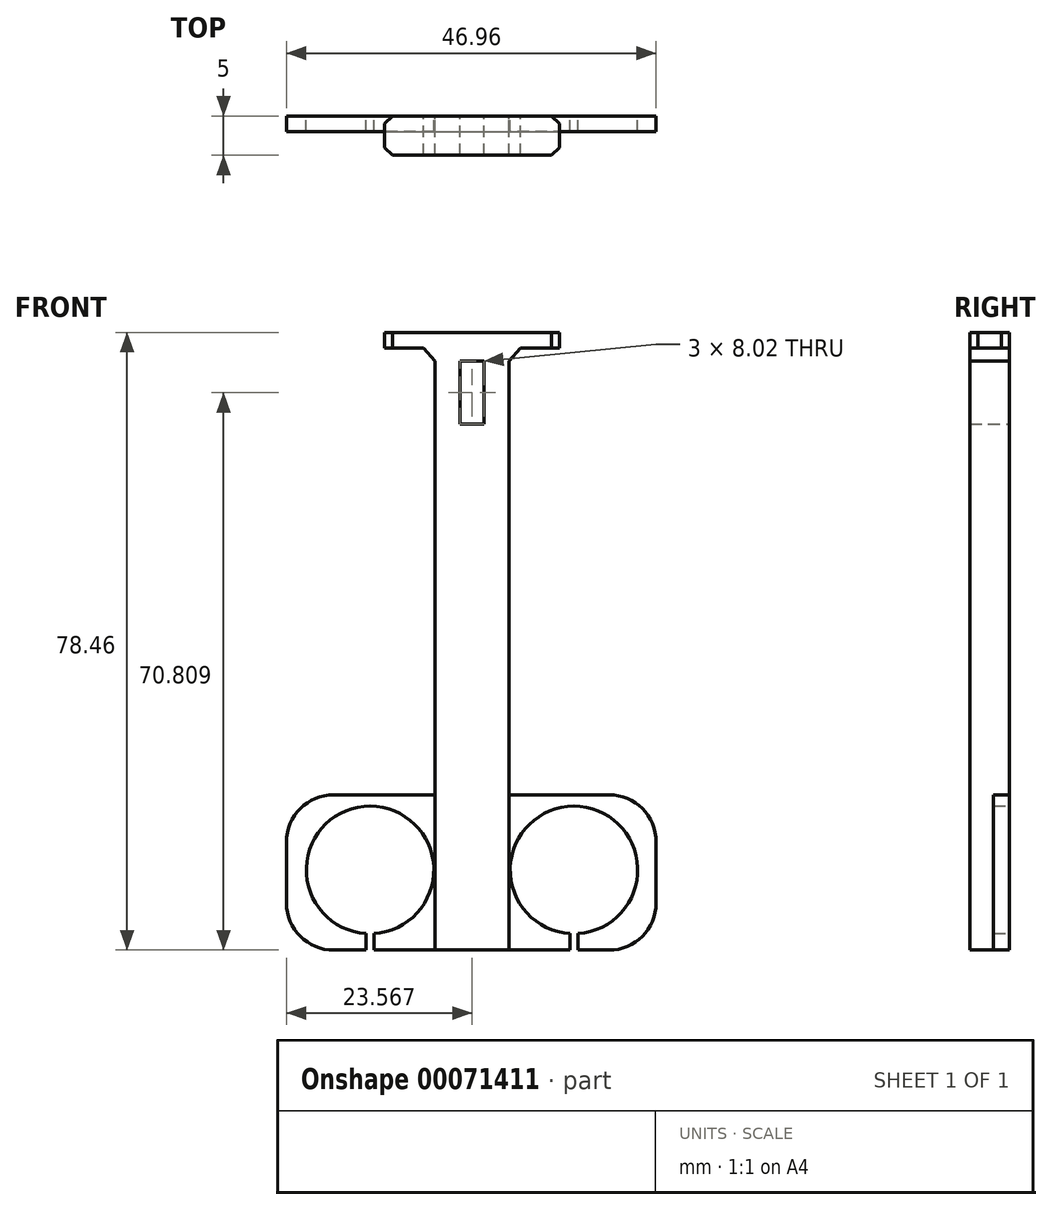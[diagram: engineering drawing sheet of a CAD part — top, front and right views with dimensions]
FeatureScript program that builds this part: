
annotation { "Feature Type Name" : "Feature", "Feature Type Description" : "" }
export const myFeature = defineFeature(function(context is Context, id is Id, definition is map)
    precondition{}
    {
        {
            var Q0;
            Q0=qCreatedBy(makeId("Front.planeOp"),FACE);
            var sketch = newSketch(context, id + "F0", { "sketchPlane" : qUnion([Q0])});
            skLineSegment(sketch, "E0.bottom", {"start": v(-5.27, 61.35) * mm, "end": v(4.07, 61.35) * mm});
            skLineSegment(sketch, "E0.top", {"start": v(-5.27, -13.44) * mm, "end": v(4.07, -13.44) * mm});
            skLineSegment(sketch, "E0.left", {"start": v(-5.27, 61.35) * mm, "end": v(-5.27, -13.44) * mm});
            skLineSegment(sketch, "E0.right", {"start": v(4.07, 61.35) * mm, "end": v(4.07, -13.44) * mm});
            skLineSegment(sketch, "E1", {"start": v(-3.37, -13.44) * mm, "end": v(-3.37, 61.35) * mm});
            skLineSegment(sketch, "E2", {"start": v(2.17, 61.35) * mm, "end": v(2.17, -13.44) * mm});
            skArc(sketch, "E3", {"start": v(-13.07, -11.37) * mm, "mid": v(-13.53, 4.81) * mm, "end": v(-14.07, -11.37) * mm});
            skArc(sketch, "E4.MirrorC", {"start": v(11.87, -11.37) * mm, "mid": v(12.33, 4.81) * mm, "end": v(12.87, -11.37) * mm});
            skLineSegment(sketch, "E5.bottom", {"start": v(-18.17, 6.25) * mm, "end": v(16.8, 6.25) * mm});
            skLineSegment(sketch, "E5.top", {"start": v(-18.17, -13.47) * mm, "end": v(-14.07, -13.47) * mm});
            skLineSegment(sketch, "E5.left", {"start": v(-24.17, 0.25) * mm, "end": v(-24.17, -7.47) * mm});
            skLineSegment(sketch, "E5.right", {"start": v(22.8, 0.25) * mm, "end": v(22.8, -7.47) * mm});
            skPoint(sketch, "E6.visualSharp", {"position": v(-24.17, 6.25) * mm});
            skArc(sketch, "E6.filletArc", {"start": v(-18.17, 6.25) * mm, "mid": v(-22.41, 4.5) * mm, "end": v(-24.17, 0.25) * mm});
            skArc(sketch, "E7.filletArc", {"start": v(22.8, 0.25) * mm, "mid": v(21.04, 4.5) * mm, "end": v(16.8, 6.25) * mm});
            skArc(sketch, "E8.filletArc", {"start": v(16.8, -13.47) * mm, "mid": v(21.04, -11.72) * mm, "end": v(22.8, -7.47) * mm});
            skPoint(sketch, "E9.visualSharp", {"position": v(-24.17, -13.47) * mm});
            skArc(sketch, "E9.filletArc", {"start": v(-24.17, -7.47) * mm, "mid": v(-22.41, -11.72) * mm, "end": v(-18.17, -13.47) * mm});
            skLineSegment(sketch, "E10", {"start": v(-14.07, -11.37) * mm, "end": v(-14.07, -13.47) * mm});
            skLineSegment(sketch, "E11", {"start": v(-14.07, -13.47) * mm, "end": v(-14.07, -11.37) * mm});
            skLineSegment(sketch, "E12", {"start": v(-13.07, -11.37) * mm, "end": v(-13.07, -13.47) * mm});
            skLineSegment(sketch, "E13", {"start": v(-13.07, -13.47) * mm, "end": v(-13.07, -11.37) * mm});
            skLineSegment(sketch, "E14.trimOffspring", {"start": v(-13.07, -13.47) * mm, "end": v(11.87, -13.47) * mm});
            skLineSegment(sketch, "E15.MirrorCS", {"start": v(11.87, -13.47) * mm, "end": v(11.87, -11.37) * mm});
            skLineSegment(sketch, "E16.MirrorCS", {"start": v(12.87, -13.47) * mm, "end": v(12.87, -11.37) * mm});
            skLineSegment(sketch, "E17.trimOffspring", {"start": v(12.87, -13.47) * mm, "end": v(16.8, -13.47) * mm});
            skLineSegment(sketch, "E18", {"start": v(4.07, 61.35) * mm, "end": v(5.55, 62.99) * mm});
            skLineSegment(sketch, "E19", {"start": v(5.55, 62.99) * mm, "end": v(9.44, 62.99) * mm});
            skLineSegment(sketch, "E20", {"start": v(9.44, 62.99) * mm, "end": v(9.44, 64.99) * mm});
            skLineSegment(sketch, "E21", {"start": v(9.44, 64.99) * mm, "end": v(10.5, 64.99) * mm});
            skLineSegment(sketch, "E22", {"start": v(10.5, 64.99) * mm, "end": v(10.5, 62.99) * mm});
            skLineSegment(sketch, "E23.MirrorCS", {"start": v(-5.27, 61.35) * mm, "end": v(-6.76, 62.99) * mm});
            skLineSegment(sketch, "E24.MirrorCS", {"start": v(-6.76, 62.99) * mm, "end": v(-10.65, 62.99) * mm});
            skLineSegment(sketch, "E25.MirrorCS", {"start": v(-10.65, 62.99) * mm, "end": v(-10.65, 64.99) * mm});
            skLineSegment(sketch, "E26.MirrorCS", {"start": v(-11.72, 64.99) * mm, "end": v(-11.72, 62.99) * mm});
            skLineSegment(sketch, "E27.MirrorCS", {"start": v(-10.65, 64.99) * mm, "end": v(-11.72, 64.99) * mm});
            skLineSegment(sketch, "E28.bottom", {"start": v(-2.1, 61.35) * mm, "end": v(0.9, 61.35) * mm});
            skLineSegment(sketch, "E28.top", {"start": v(-2.1, 53.33) * mm, "end": v(0.9, 53.33) * mm});
            skLineSegment(sketch, "E28.left", {"start": v(-2.1, 61.35) * mm, "end": v(-2.1, 53.33) * mm});
            skLineSegment(sketch, "E28.right", {"start": v(0.9, 61.35) * mm, "end": v(0.9, 53.33) * mm});
            skPoint(sketch, "E28.middle", {"position": v(-0.6, 57.34) * mm});
            skLineSegment(sketch, "E29", {"start": v(-10.65, 62.99) * mm, "end": v(-11.72, 62.99) * mm});
            skLineSegment(sketch, "E30", {"start": v(-10.65, 64.99) * mm, "end": v(9.44, 64.99) * mm});
            skLineSegment(sketch, "E31", {"start": v(9.44, 62.99) * mm, "end": v(10.5, 62.99) * mm});
            skLineSegment(sketch, "E32", {"start": v(-6.76, 62.99) * mm, "end": v(5.55, 62.99) * mm});
            skLineSegment(sketch, "E33", {"start": v(-5.27, -11.42) * mm, "end": v(-3.37, -11.42) * mm});
            skLineSegment(sketch, "E34", {"start": v(2.17, -11.42) * mm, "end": v(4.07, -11.42) * mm});
            skSolve(sketch);
        }
        {
            var Q0;
            Q0=makeQuery(id+"F0.imprint","IMPRINT",FACE,{"disambiguationData":[TD([[makeQuery(id+"F0.imprint","IMPRINT",EDGE,{"derivedFrom":sQuery(id+"F0.wireOp",EDGE,"E3")}),-1.0]])]});
            extrude(context, id + "F1", {"entities" : qUnion([Q0]), "depth" : 2 * mm});
        }
        {
            var Q0;
            {var subQ1=sQuery(id+"F0.wireOp",EDGE,"E0.bottom");var subQ3=sQuery(id+"F0.wireOp",EDGE,"E1");var subQ4=makeQuery(id+"F0.imprint","INTERSECT",VERTEX,{"derivedFrom":[subQ1,subQ3]});Q0=makeQuery(id+"F0.imprint","IMPRINT",FACE,{"disambiguationData":[TD([[makeQuery(id+"F0.imprint","IMPRINT",EDGE,{"disambiguationData":[TD([[subQ4,1.0]])],"derivedFrom":subQ3}),1.0]])]});}
            var Q1;
            Q1=makeQuery(id+"F0.imprint","IMPRINT",FACE,{"disambiguationData":[TD([[makeQuery(id+"F0.imprint","IMPRINT",EDGE,{"derivedFrom":sQuery(id+"F0.wireOp",EDGE,"E28.top")}),-1.0]])]});
            var Q2;
            {var subQ1=sQuery(id+"F0.wireOp",EDGE,"E0.bottom");var subQ3=sQuery(id+"F0.wireOp",EDGE,"E2");var subQ4=makeQuery(id+"F0.imprint","INTERSECT",VERTEX,{"derivedFrom":[subQ1,subQ3]});Q2=makeQuery(id+"F0.imprint","IMPRINT",FACE,{"disambiguationData":[TD([[makeQuery(id+"F0.imprint","IMPRINT",EDGE,{"disambiguationData":[TD([[subQ4,-1.0]])],"derivedFrom":subQ3}),1.0]])]});}
            var Q3;
            Q3=makeQuery(id+"F0.imprint","IMPRINT",FACE,{"disambiguationData":[TD([[makeQuery(id+"F0.imprint","IMPRINT",EDGE,{"derivedFrom":sQuery(id+"F0.wireOp",EDGE,"E28.bottom")}),-1.0]])]});
            var Q4;
            {var subQ0=sQuery(id+"F0.wireOp",EDGE,"E18");Q4=makeQuery(id+"F0.imprint","IMPRINT",FACE,{"disambiguationData":[TD([[makeQuery(id+"F0.imprint","IMPRINT",EDGE,{"derivedFrom":subQ0}),1.0]])]});}
            var Q5;
            Q5=makeQuery(id+"F0.imprint","IMPRINT",FACE,{"disambiguationData":[TD([[makeQuery(id+"F0.imprint","IMPRINT",EDGE,{"derivedFrom":sQuery(id+"F0.wireOp",EDGE,"E25.MirrorCS")}),1.0]])]});
            var Q6;
            Q6=makeQuery(id+"F0.imprint","IMPRINT",FACE,{"disambiguationData":[TD([[makeQuery(id+"F0.imprint","IMPRINT",EDGE,{"derivedFrom":sQuery(id+"F0.wireOp",EDGE,"E20")}),-1.0]])]});
            var Q7;
            Q7=makeQuery(id+"F0.imprint","IMPRINT",FACE,{"disambiguationData":[TD([[makeQuery(id+"F0.imprint","IMPRINT",EDGE,{"derivedFrom":sQuery(id+"F0.wireOp",EDGE,"E19")}),1.0]])]});
            var Q8;
            {var subQ0=sQuery(id+"F0.wireOp",EDGE,"E33");Q8=makeQuery(id+"F0.imprint","IMPRINT",FACE,{"disambiguationData":[TD([[makeQuery(id+"F0.imprint","IMPRINT",EDGE,{"derivedFrom":subQ0}),1.0]])]});}
            var Q9;
            {var subQ4=sQuery(id+"F0.wireOp",EDGE,"E1");var subQ5=sQuery(id+"F0.wireOp",EDGE,"E0.top");var subQ6=makeQuery(id+"F0.imprint","INTERSECT",VERTEX,{"derivedFrom":[subQ5,subQ4]});Q9=makeQuery(id+"F0.imprint","IMPRINT",FACE,{"disambiguationData":[TD([[makeQuery(id+"F0.imprint","IMPRINT",EDGE,{"disambiguationData":[TD([[subQ6,-1.0]])],"derivedFrom":subQ5}),1.0]])]});}
            var Q10;
            {var subQ0=sQuery(id+"F0.wireOp",EDGE,"E34");Q10=makeQuery(id+"F0.imprint","IMPRINT",FACE,{"disambiguationData":[TD([[makeQuery(id+"F0.imprint","IMPRINT",EDGE,{"derivedFrom":subQ0}),1.0]])]});}
            var Q11;
            {var subQ5=sQuery(id+"F0.wireOp",EDGE,"E33");Q11=makeQuery(id+"F0.imprint","IMPRINT",FACE,{"disambiguationData":[TD([[makeQuery(id+"F0.imprint","IMPRINT",EDGE,{"derivedFrom":subQ5}),-1.0]])]});}
            var Q12;
            {var subQ5=sQuery(id+"F0.wireOp",EDGE,"E34");Q12=makeQuery(id+"F0.imprint","IMPRINT",FACE,{"disambiguationData":[TD([[makeQuery(id+"F0.imprint","IMPRINT",EDGE,{"derivedFrom":subQ5}),-1.0]])]});}
            extrude(context, id + "F2", {"entities" : qUnion([Q0, Q1, Q2, Q3, Q4, Q5, Q6, Q7, Q8, Q9, Q10, Q11, Q12]), "operationType" : NewBodyOperationType.ADD, "depth" : 5 * mm});
        }
        {
            var Q0;
            Q0=makeQuery(id+"F2.opExtrude","CAP_EDGE",EDGE,{"disambiguationData":[OSD([sQuery(id+"F0.wireOp",EDGE,"E22")])],"isStart":true});
            var Q1;
            Q1=makeQuery(id+"F2.opExtrude","CAP_EDGE",EDGE,{"disambiguationData":[OSD([sQuery(id+"F0.wireOp",EDGE,"E22")])],"isStart":false});
            var Q2;
            Q2=makeQuery(id+"F2.opExtrude","CAP_EDGE",EDGE,{"disambiguationData":[OSD([sQuery(id+"F0.wireOp",EDGE,"E26.MirrorCS")])],"isStart":false});
            var Q3;
            Q3=makeQuery(id+"F2.opExtrude","CAP_EDGE",EDGE,{"disambiguationData":[OSD([sQuery(id+"F0.wireOp",EDGE,"E26.MirrorCS")])],"isStart":true});
            chamfer(context, id + "F3", {"entities" : qUnion([Q0, Q1, Q2, Q3]), "width" : 1 * mm, "tangentPropagation" : true});
        }
    });
